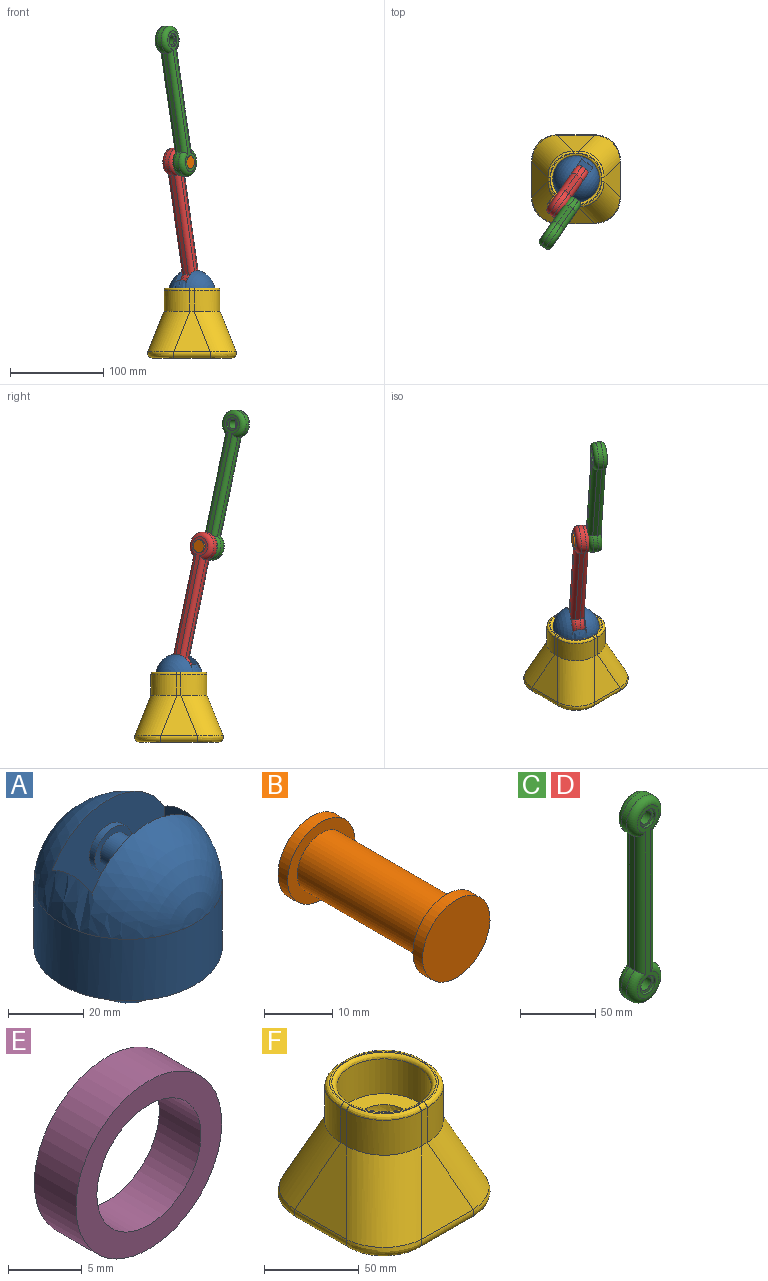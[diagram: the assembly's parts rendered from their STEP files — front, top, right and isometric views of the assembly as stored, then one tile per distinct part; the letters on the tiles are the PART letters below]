
ASSEMBLY  parts=6 mates=6
PART A: 14 faces, bbox 50x50x60 mm
  f0: sphere r=25mm, area 3160.2mm2, adj f1,f4,f5,f6,f7
  f1: cylinder r=25mm len=50mm, axis (0,0,1), area 3141.6mm2, adj f0,f2
  f2: plane 50x50mm, normal (0,0,-1), area 1256.6mm2, adj f1,f3
  f3: sphere r=15mm, area 1413.7mm2, adj f2
  f4: plane 28.56x15mm, normal (-1,0,0), area 417.6mm2, adj f0,f5,f7,f8
  f5: plane 42x38.85mm, normal (0,1,0), area 1326mm2, adj f0,f4,f6,f8,f9
  f6: plane 28.56x15mm, normal (1,0,0), area 417.6mm2, adj f0,f5,f7,f8
  f7: plane 42x38.85mm, normal (0,-1,0), area 1326mm2, adj f0,f4,f6,f8,f12
  f8: plane 42x15mm, normal (0,0,1), area 630mm2, adj f4,f5,f6,f7
  f9: cylinder r=7mm len=14mm, axis (0,-1,0), area 88mm2, adj f5,f10
  f10: plane 14x14mm, normal (0,1,0), area 75.4mm2, adj f9,f11
  f11: cylinder r=5mm len=11mm, axis (0,-1,0), area 345.6mm2, adj f10,f13
  f12: cylinder r=7mm len=14mm, axis (0,1,0), area 88mm2, adj f7,f13
  f13: plane 14x14mm, normal (0,-1,0), area 75.4mm2, adj f11,f12
PART B: 7 faces, bbox 14x30x14 mm
  f0: plane 14x14mm, normal (0,1,0), area 75.4mm2, adj f1,f6
  f1: cylinder r=5mm len=26mm, axis (0,1,0), area 816.8mm2, adj f0,f2
  f2: plane 14x14mm, normal (0,-1,0), area 75.4mm2, adj f1,f3
  f3: cylinder r=7mm len=14mm, axis (0,1,0), area 88mm2, adj f2,f4
  f4: plane 14x14mm, normal (0,1,0), area 153.9mm2, adj f3
  f5: plane 14x14mm, normal (0,-1,0), area 153.9mm2, adj f6
  f6: cylinder r=7mm len=14mm, axis (0,1,0), area 88mm2, adj f0,f5
PART C: 24 faces, bbox 32.5x15x167.5 mm
  f0: cylinder r=5mm len=11mm, axis (0,-1,0), area 345.6mm2, adj f19,f22
  f1: cylinder r=5mm len=11mm, axis (0,-1,0), area 345.6mm2, adj f17,f20
  f2: plane 109.02x5mm, normal (1,0,0), area 545.1mm2, adj f3,f5,f8,f12
  f3: cylinder r=15mm len=30mm, axis (0,1,0), area 392.7mm2, adj f2,f4,f9,f13
  f4: plane 109.02x5mm, normal (-1,0,0), area 545.1mm2, adj f3,f5,f11,f15
  f5: cylinder r=15mm len=30mm, axis (0,1,0), area 392.7mm2, adj f2,f4,f10,f14
  f6: plane 155x20mm, normal (0,-1,0), area 896.5mm2, adj f12,f13,f14,f15,f16,f18
  f7: plane 155x20mm, normal (0,1,0), area 896.5mm2, adj f8,f9,f10,f11,f21,f23
  f8: cylinder r=5mm len=115.64mm, axis (0,0,1), area 874.1mm2, adj f2,f7,f9,f10
  f9: torus R=10mm, axis (0,-1,0), area 558mm2, adj f3,f7,f8,f11
  f10: torus R=10mm, axis (0,-1,0), area 558mm2, adj f5,f7,f8,f11
  f11: cylinder r=5mm len=115.64mm, axis (0,0,-1), area 874.1mm2, adj f4,f7,f9,f10
  f12: cylinder r=5mm len=115.64mm, axis (0,0,-1), area 874.1mm2, adj f2,f6,f13,f14
  f13: torus R=10mm, axis (0,-1,0), area 558mm2, adj f3,f6,f12,f15
  f14: torus R=10mm, axis (0,-1,0), area 558mm2, adj f5,f6,f12,f15
  f15: cylinder r=5mm len=115.64mm, axis (0,0,1), area 874.1mm2, adj f4,f6,f13,f14
  f16: cylinder r=7mm len=14mm, axis (0,-1,0), area 88mm2, adj f6,f17
  f17: plane 14x14mm, normal (0,-1,0), area 75.4mm2, adj f1,f16
  f18: cylinder r=7mm len=14mm, axis (0,-1,0), area 88mm2, adj f6,f19
  f19: plane 14x14mm, normal (0,-1,0), area 75.4mm2, adj f0,f18
  f20: plane 14x14mm, normal (0,1,0), area 75.4mm2, adj f1,f21
  f21: cylinder r=7mm len=14mm, axis (0,1,0), area 88mm2, adj f7,f20
  f22: plane 14x14mm, normal (0,1,0), area 75.4mm2, adj f0,f23
  f23: cylinder r=7mm len=14mm, axis (0,1,0), area 88mm2, adj f7,f22
PART D: same geometry as C
PART E: 4 faces, bbox 14x4x14 mm
  f0: cylinder r=5mm len=10mm, axis (0,-1,0), area 125.7mm2, adj f2,f3
  f1: cylinder r=7mm len=14mm, axis (0,-1,0), area 175.9mm2, adj f2,f3
  f2: plane 14x14mm, normal (0,1,0), area 75.4mm2, adj f0,f1
  f3: plane 14x14mm, normal (0,-1,0), area 75.4mm2, adj f0,f1
PART F: 41 faces, bbox 100.2x100.2x75 mm
  f0: plane 27.5x27.5mm, normal (0,0,1), area 30.8mm2, adj f32,f33,f34,f35
  f1: plane 27.5x27.5mm, normal (0,0,1), area 30.8mm2, adj f32,f34,f36,f38
  f2: plane 27.5x27.5mm, normal (0,0,1), area 30.8mm2, adj f32,f38,f39,f40
  f3: plane 85.23x85.23mm, normal (0,0,-1), area 6821.3mm2, adj f8,f9,f10,f11,f13,f15,f17,f19
  f4: plane 43.14x38.81mm, normal (0,-0.93,0.37), area 1001.3mm2, adj f10,f14,f18,f21
  f5: plane 43.14x38.81mm, normal (0.93,0,0.37), area 1001.3mm2, adj f8,f16,f18,f23
  f6: plane 43.14x38.81mm, normal (0,0.93,0.37), area 1001.3mm2, adj f9,f12,f16,f25
  f7: plane 43.14x38.81mm, normal (-0.93,0,0.37), area 1001.3mm2, adj f11,f12,f14,f28
  f8: cylinder r=5mm len=38.81mm, axis (0,-1,0), area 378.6mm2, adj f3,f5,f17,f19
  f9: cylinder r=5mm len=38.81mm, axis (-1,0,0), area 378.6mm2, adj f3,f6,f13,f17
  f10: cylinder r=5mm len=38.81mm, axis (-1,0,0), area 378.6mm2, adj f3,f4,f15,f19
  f11: cylinder r=5mm len=38.81mm, axis (0,-1,0), area 378.6mm2, adj f3,f7,f13,f15
  f12: cylinder r=30mm len=49.81mm, axis (0.35,-0.35,0.87), area 2110.3mm2, adj f6,f7,f13,f26
  f13: bspline ~34.54x34.54mm, area 430.9mm2, adj f3,f9,f11,f12
  f14: cylinder r=30mm len=49.81mm, axis (-0.35,-0.35,-0.87), area 2110.3mm2, adj f4,f7,f15,f20
  f15: bspline ~28.22x28.22mm, area 430.9mm2, adj f3,f10,f11,f14
  f16: cylinder r=30mm len=49.81mm, axis (0.35,0.35,-0.87), area 2110.3mm2, adj f5,f6,f17,f24
  f17: bspline ~28.22x28.22mm, area 430.9mm2, adj f3,f8,f9,f16
  f18: cylinder r=30mm len=49.81mm, axis (-0.35,0.35,0.87), area 2110.3mm2, adj f4,f5,f19,f22
  f19: bspline ~34.54x34.54mm, area 430.9mm2, adj f3,f8,f10,f18
  f20: extruded ~27.85x27.85mm, area 990.3mm2, adj f14,f21,f28,f37
  f21: plane 22.5x4.29mm, normal (0,-1,0), area 96.6mm2, adj f4,f20,f22,f35
  f22: extruded ~27.85x27.85mm, area 990.3mm2, adj f18,f21,f23,f33
  f23: plane 22.5x4.29mm, normal (1,0,0), area 96.6mm2, adj f5,f22,f24,f34
  f24: extruded ~27.85x27.85mm, area 990.3mm2, adj f16,f23,f25,f36
  f25: plane 22.5x4.29mm, normal (0,1,0), area 96.6mm2, adj f6,f24,f26,f38
  f26: extruded ~27.85x27.85mm, area 990.3mm2, adj f12,f25,f28,f40
  f27: cylinder r=25mm len=50mm, axis (0,0,-1), area 3534.3mm2, adj f31,f32
  f28: plane 22.5x4.29mm, normal (-1,0,0), area 96.6mm2, adj f7,f20,f26,f39
  f29: plane 27.5x27.5mm, normal (0,0,1), area 30.8mm2, adj f32,f35,f37,f39
  f30: sphere r=15mm, area 1413.7mm2, adj f31
  f31: plane 50x50mm, normal (0,0,1), area 1256.6mm2, adj f27,f30
  f32: torus R=27.5mm, axis (0,0,1), area 639.3mm2, adj f0,f1,f2,f27,f29
  f33: bspline ~32.23x32.23mm, area 167.2mm2, adj f0,f22,f34,f35
  f34: cylinder r=2.5mm len=4.29mm, axis (0,-1,0), area 16.9mm2, adj f0,f1,f23,f33,f36
  f35: cylinder r=2.5mm len=4.29mm, axis (-1,0,0), area 16.9mm2, adj f0,f21,f29,f33,f37
  f36: bspline ~32.23x32.23mm, area 167.2mm2, adj f1,f24,f34,f38
  f37: bspline ~32.23x32.23mm, area 167.2mm2, adj f20,f29,f35,f39
  f38: cylinder r=2.5mm len=4.29mm, axis (1,0,0), area 16.9mm2, adj f1,f2,f25,f36,f40
  f39: cylinder r=2.5mm len=4.29mm, axis (0,1,0), area 16.9mm2, adj f2,f28,f29,f37,f40
  f40: bspline ~32.23x32.23mm, area 167.2mm2, adj f2,f26,f38,f39
PLACE A rot(axis=(0,0,1),55.2deg) t=(84.89,41.69,23.84)mm
PLACE B rot(axis=(-0.88,-0.46,-0.11),173.5deg) t=(-215.72,-238.08,98.62)mm
PLACE C rot(axis=(-0.46,0.88,0.06),167.5deg) t=(27.86,36.22,329.48)mm
PLACE D rot(axis=(-0.88,-0.46,-0.11),173.6deg) t=(-108.61,-163.9,130.03)mm
PLACE E rot(axis=(0.73,0.38,-0.57),146.8deg) t=(-108.09,-90.17,474.3)mm
PLACE F t=(-67.8,-69.91,-46.16)mm fixed
MATE revolute E.f0 <-> C.f1  axis (0.82,-0.57,0) through (-30.11,-50.81,163.75)mm
MATE revolute D.f1 <-> A.f9  axis (0.82,-0.57,0) through (-13.28,-23.05,32.69)mm
MATE planar A.f1 <-> F.f27  axis (0,0,-1) through (-17.8,-19.91,3.84)mm
MATE ball A.f1 <-> F.f27  axis (0,0,1) through (-17.8,-19.91,3.84)mm
MATE fastened E.f0 <-> D.f0  axis (-0.82,0.57,0) through (-31.76,-49.67,163.75)mm
MATE fastened B.f1 <-> C.f1  axis (-0.82,0.57,0) through (-21.08,-57.09,163.75)mm
